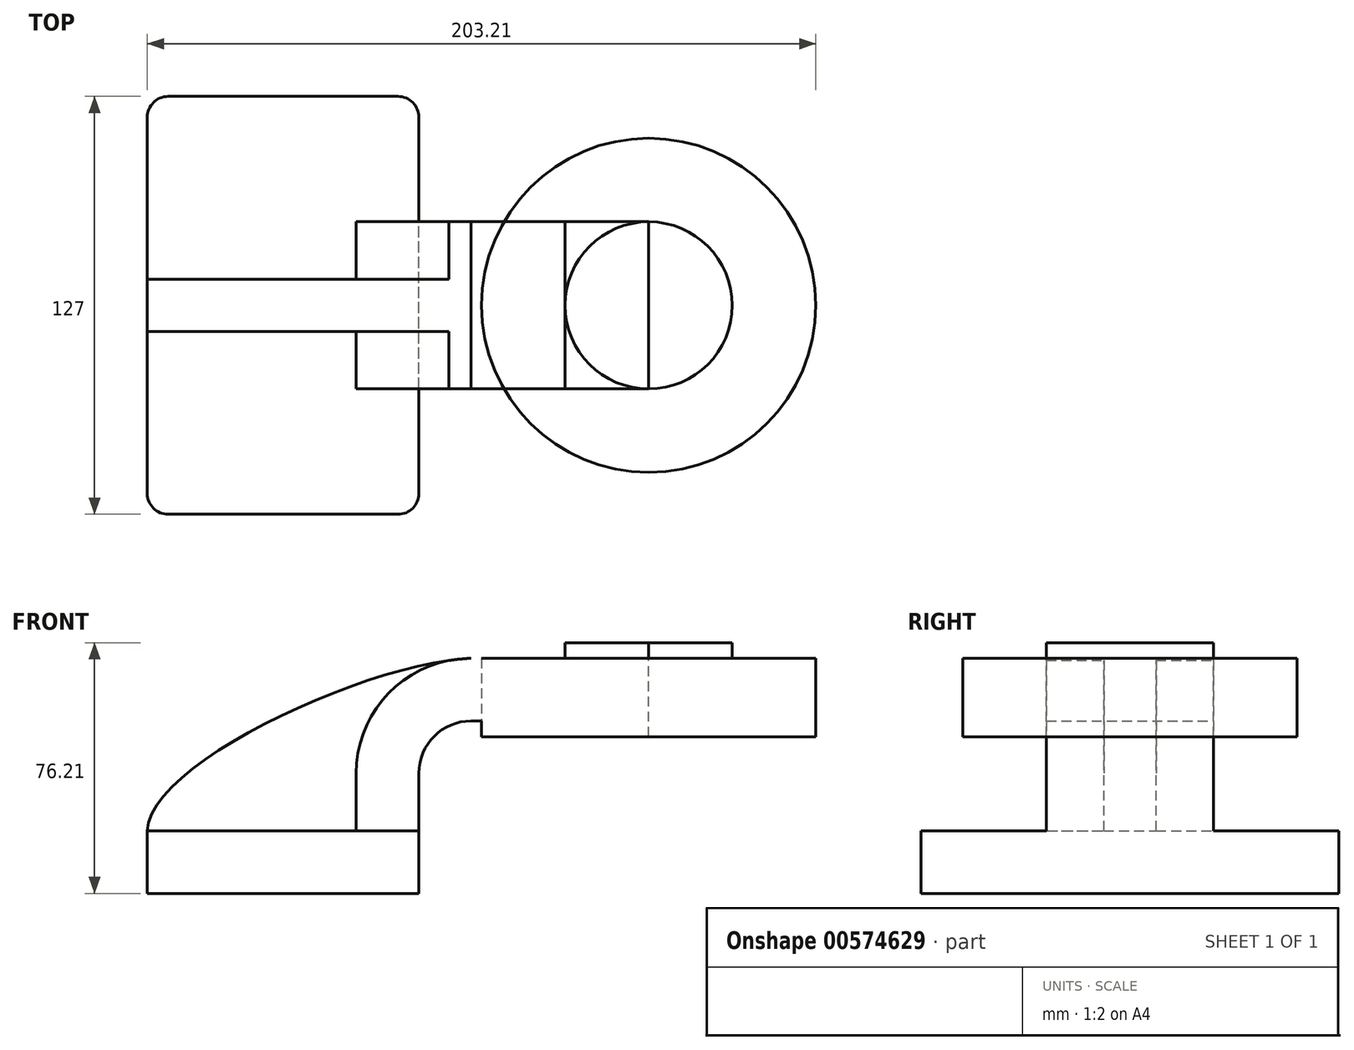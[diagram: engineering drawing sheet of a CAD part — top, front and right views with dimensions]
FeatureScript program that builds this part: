
annotation { "Feature Type Name" : "Feature", "Feature Type Description" : "" }
export const myFeature = defineFeature(function(context is Context, id is Id, definition is map)
    precondition{}
    {
        {
            var Q0;
            Q0=qCreatedBy(makeId("Front.planeOp"),FACE);
            var sketch = newSketch(context, id + "F0", { "sketchPlane" : qUnion([Q0])});
            skLineSegment(sketch, "E0.bottom", {"start": v(-41.28, -9.53) * mm, "end": v(41.28, -9.53) * mm});
            skLineSegment(sketch, "E0.top", {"start": v(-41.28, 9.52) * mm, "end": v(41.28, 9.52) * mm});
            skLineSegment(sketch, "E0.left", {"start": v(-41.28, -9.53) * mm, "end": v(-41.28, 9.53) * mm});
            skLineSegment(sketch, "E0.right", {"start": v(41.28, -9.53) * mm, "end": v(41.28, 9.52) * mm});
            skPoint(sketch, "E0.middle", {"position": v(0, 0) * mm});
            skLineSegment(sketch, "E1.bottom", {"start": v(60.33, 38.1) * mm, "end": v(111.12, 38.1) * mm});
            skLineSegment(sketch, "E1.top", {"start": v(60.32, 66.68) * mm, "end": v(111.12, 66.68) * mm});
            skLineSegment(sketch, "E1.left", {"start": v(60.33, 38.1) * mm, "end": v(60.33, 66.68) * mm});
            skLineSegment(sketch, "E1.right", {"start": v(111.12, 38.1) * mm, "end": v(111.12, 66.68) * mm});
            skPoint(sketch, "E1.middle", {"position": v(85.72, 52.39) * mm});
            skLineSegment(sketch, "E2", {"start": v(41.28, 9.52) * mm, "end": v(41.28, 27) * mm});
            skArc(sketch, "E3", {"start": v(41.27, 27) * mm, "mid": v(45.92, 38.23) * mm, "end": v(57.15, 42.88) * mm});
            skLineSegment(sketch, "E4", {"start": v(57.15, 42.88) * mm, "end": v(85.8, 42.88) * mm});
            skLineSegment(sketch, "E5", {"start": v(85.8, 42.88) * mm, "end": v(71.53, 42.88) * mm});
            skLineSegment(sketch, "E6.0", {"start": v(57.15, 61.93) * mm, "end": v(85.72, 61.93) * mm});
            skArc(sketch, "E6.1", {"start": v(22.22, 27) * mm, "mid": v(32.45, 51.7) * mm, "end": v(57.15, 61.93) * mm});
            skLineSegment(sketch, "E6.2", {"start": v(22.22, 9.52) * mm, "end": v(22.22, 27) * mm});
            skLineSegment(sketch, "E7", {"start": v(85.72, 48.81) * mm, "end": v(85.72, 66.68) * mm});
            skFitSpline(sketch, "E8", {"points": [v(-41.28, 9.53) * mm, v(57.15, 61.93) * mm], "startDerivative": vector(1.11, 60.49) * mm, "endDerivative": vector(98.12, 4.67) * mm});
            skSolve(sketch);
        }
        {
            var Q0;
            Q0=makeQuery(id+"F0.imprint","IMPRINT",FACE,{"disambiguationData":[TD([[makeQuery(id+"F0.imprint","IMPRINT",EDGE,{"derivedFrom":sQuery(id+"F0.wireOp",EDGE,"E0.bottom")}),1.0]])]});
            extrude(context, id + "F1", {"entities" : qUnion([Q0]), "endBound" : BoundingType.SYMMETRIC, "depth" : 127 * mm, "offsetDistance" : 25.4 * mm});
        }
        {
            var Q0;
            {var subQ1=sQuery(id+"F0.wireOp",EDGE,"E2");Q0=makeQuery(id+"F0.imprint","IMPRINT",FACE,{"disambiguationData":[TD([[makeQuery(id+"F0.imprint","IMPRINT",EDGE,{"derivedFrom":subQ1}),1.0]])]});}
            var Q1;
            {var subQ8=sQuery(id+"F0.wireOp",EDGE,"E1.bottom");Q1=makeQuery(id+"F0.imprint","IMPRINT",FACE,{"disambiguationData":[TD([[makeQuery(id+"F0.imprint","IMPRINT",EDGE,{"derivedFrom":subQ8}),1.0]])]});}
            extrude(context, id + "F2", {"entities" : qUnion([Q0, Q1]), "operationType" : NewBodyOperationType.ADD, "endBound" : BoundingType.SYMMETRIC, "depth" : 50.8 * mm, "offsetDistance" : 25.4 * mm});
        }
        {
            var Q0;
            {var subQ3=sQuery(id+"F0.wireOp",EDGE,"E6.2");Q0=makeQuery(id+"F0.imprint","IMPRINT",FACE,{"disambiguationData":[TD([[makeQuery(id+"F0.imprint","IMPRINT",EDGE,{"derivedFrom":subQ3}),1.0]])]});}
            extrude(context, id + "F3", {"entities" : qUnion([Q0]), "operationType" : NewBodyOperationType.ADD, "endBound" : BoundingType.SYMMETRIC, "depth" : 15.88 * mm, "offsetDistance" : 25.4 * mm});
        }
        {
            var Q0;
            {var subQ8=sQuery(id+"F0.wireOp",EDGE,"E1.bottom");Q0=makeQuery(id+"F0.imprint","IMPRINT",FACE,{"disambiguationData":[TD([[makeQuery(id+"F0.imprint","IMPRINT",EDGE,{"derivedFrom":subQ8}),1.0]])]});}
            var Q1;
            Q1=sQuery(id+"F0.wireOp",EDGE,"E1.right");
            revolve(context, id + "F4", {"entities" : qUnion([Q0]), "axis" : qUnion([Q1]), "revolveType" : RevolveType.FULL});
        }
        {
            var Q0;
            Q0=makeQuery(id+"F1.opExtrude","CAP_EDGE",EDGE,{"disambiguationData":[OSD([sQuery(id+"F0.wireOp",EDGE,"E0.left")])],"isStart":false});
            var Q1;
            Q1=makeQuery(id+"F1.opExtrude","CAP_EDGE",EDGE,{"disambiguationData":[OSD([sQuery(id+"F0.wireOp",EDGE,"E0.right")])],"isStart":false});
            var Q2;
            Q2=makeQuery(id+"F1.opExtrude","CAP_EDGE",EDGE,{"disambiguationData":[OSD([sQuery(id+"F0.wireOp",EDGE,"E0.right")])],"isStart":true});
            var Q3;
            Q3=makeQuery(id+"F1.opExtrude","CAP_EDGE",EDGE,{"disambiguationData":[OSD([sQuery(id+"F0.wireOp",EDGE,"E0.left")])],"isStart":true});
            fillet(context, id + "F5", {"entities" : qUnion([Q0, Q1, Q2, Q3]), "radius" : 6.35 * mm, "tangentPropagation" : true, "allowEdgeOverflow" : false});
        }
    });
